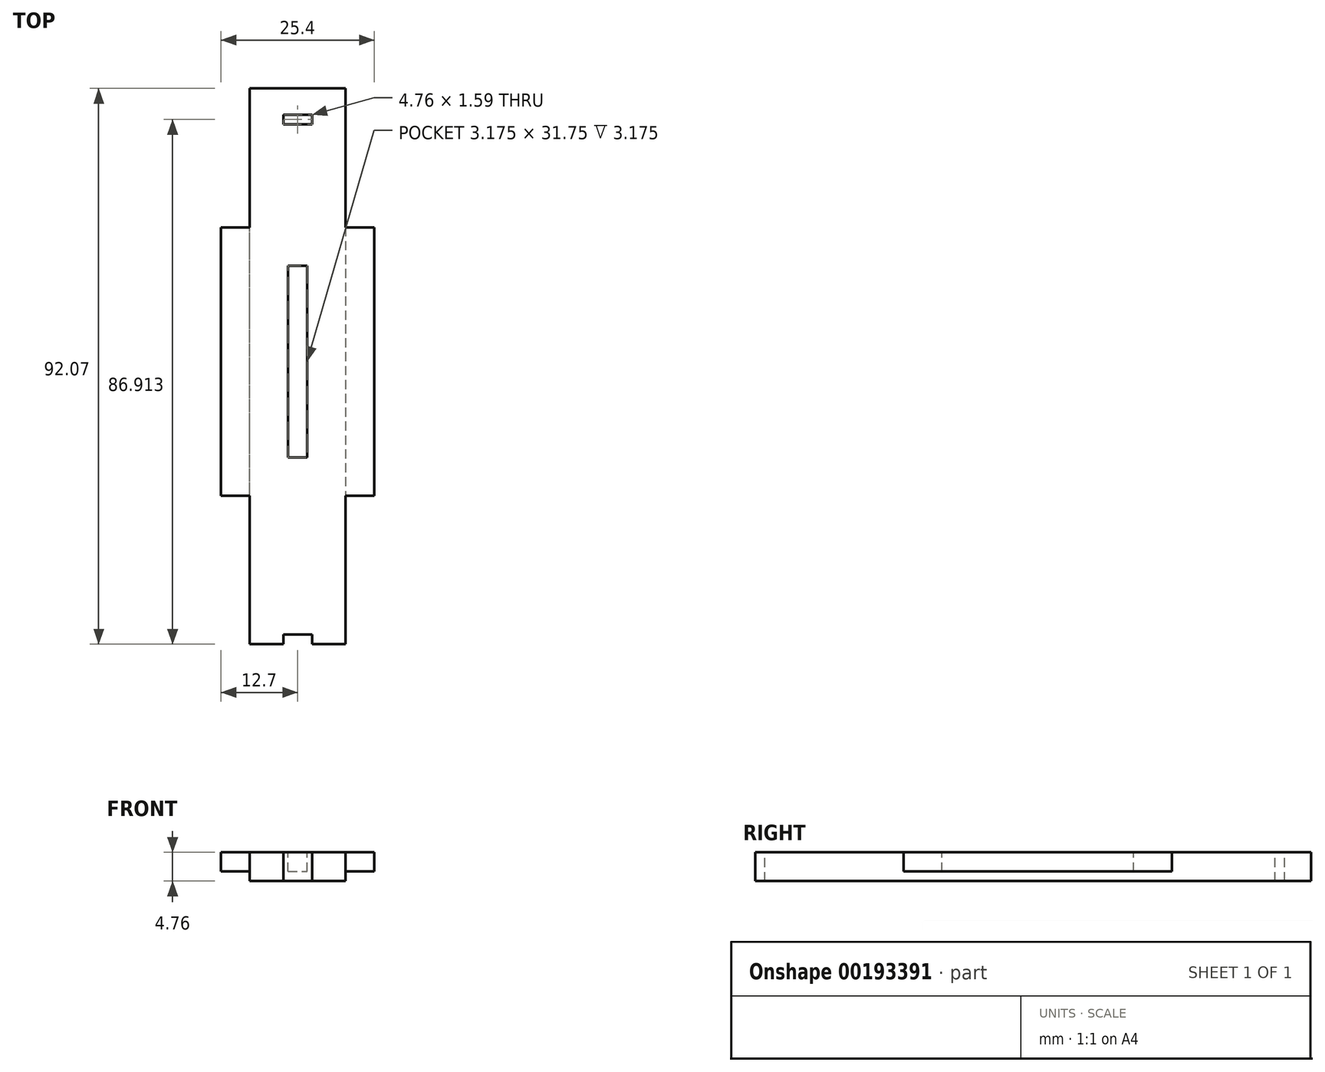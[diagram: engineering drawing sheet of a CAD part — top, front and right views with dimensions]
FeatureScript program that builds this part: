
annotation { "Feature Type Name" : "Feature", "Feature Type Description" : "" }
export const myFeature = defineFeature(function(context is Context, id is Id, definition is map)
    precondition{}
    {
        {
            var Q0;
            Q0=qCreatedBy(makeId("Top.planeOp"),FACE);
            var sketch = newSketch(context, id + "F0", { "sketchPlane" : qUnion([Q0])});
            skLineSegment(sketch, "E0", {"start": v(-7.94, 49.21) * mm, "end": v(7.94, 49.21) * mm});
            skLineSegment(sketch, "E1", {"start": v(7.94, 49.21) * mm, "end": v(7.94, 26.2) * mm});
            skLineSegment(sketch, "E2", {"start": v(7.94, 26.2) * mm, "end": v(12.7, 26.2) * mm});
            skLineSegment(sketch, "E3", {"start": v(12.7, 26.2) * mm, "end": v(12.7, -18.26) * mm});
            skLineSegment(sketch, "E4", {"start": v(12.7, -18.26) * mm, "end": v(7.94, -18.26) * mm});
            skLineSegment(sketch, "E5", {"start": v(7.94, -18.26) * mm, "end": v(7.94, -42.86) * mm});
            skLineSegment(sketch, "E6", {"start": v(7.94, -42.86) * mm, "end": v(-7.94, -42.86) * mm});
            skLineSegment(sketch, "E7", {"start": v(-7.94, -42.86) * mm, "end": v(-7.94, -18.26) * mm});
            skLineSegment(sketch, "E8", {"start": v(-7.94, -18.26) * mm, "end": v(-12.7, -18.26) * mm});
            skLineSegment(sketch, "E9", {"start": v(-12.7, -18.26) * mm, "end": v(-12.7, 26.2) * mm});
            skLineSegment(sketch, "E10", {"start": v(-12.7, 26.2) * mm, "end": v(-7.94, 26.2) * mm});
            skLineSegment(sketch, "E11", {"start": v(-7.94, 26.2) * mm, "end": v(-7.94, 49.21) * mm});
            skSolve(sketch);
        }
        {
            var Q0;
            Q0 = qSketchRegion(id + "F0", true);
            extrude(context, id + "F1", {"entities" : qUnion([Q0]), "depth" : 3.17 * mm});
        }
        {
            var Q0;
            Q0=makeQuery(id+"F1.opExtrude","CAP_FACE",FACE,{"disambiguationData":[OSD([sQuery(id+"F0.wireOp",EDGE,"E0"),sQuery(id+"F0.wireOp",EDGE,"E1"),sQuery(id+"F0.wireOp",EDGE,"E2"),sQuery(id+"F0.wireOp",EDGE,"E3"),sQuery(id+"F0.wireOp",EDGE,"E4"),sQuery(id+"F0.wireOp",EDGE,"E5"),sQuery(id+"F0.wireOp",EDGE,"E6"),sQuery(id+"F0.wireOp",EDGE,"E7"),sQuery(id+"F0.wireOp",EDGE,"E8"),sQuery(id+"F0.wireOp",EDGE,"E9"),sQuery(id+"F0.wireOp",EDGE,"E10"),sQuery(id+"F0.wireOp",EDGE,"E11")])],"isStart":true});
            var sketch = newSketch(context, id + "F2", { "sketchPlane" : qUnion([Q0])});
            skLineSegment(sketch, "E12.bottom", {"start": v(7.94, -49.21) * mm, "end": v(-7.94, -49.21) * mm});
            skLineSegment(sketch, "E12.top", {"start": v(7.94, 42.86) * mm, "end": v(-7.94, 42.86) * mm});
            skLineSegment(sketch, "E12.left", {"start": v(7.94, -49.21) * mm, "end": v(7.94, 42.86) * mm});
            skLineSegment(sketch, "E12.right", {"start": v(-7.94, -49.21) * mm, "end": v(-7.94, 42.86) * mm});
            skSolve(sketch);
        }
        {
            var Q0;
            Q0 = qSketchRegion(id + "F2", true);
            extrude(context, id + "F3", {"entities" : qUnion([Q0]), "operationType" : NewBodyOperationType.ADD, "depth" : 1.59 * mm});
        }
        {
            var Q0;
            Q0=makeQuery(id+"F1.opExtrude","CAP_FACE",FACE,{"disambiguationData":[OSD([sQuery(id+"F0.wireOp",EDGE,"E0"),sQuery(id+"F0.wireOp",EDGE,"E1"),sQuery(id+"F0.wireOp",EDGE,"E2"),sQuery(id+"F0.wireOp",EDGE,"E3"),sQuery(id+"F0.wireOp",EDGE,"E4"),sQuery(id+"F0.wireOp",EDGE,"E5"),sQuery(id+"F0.wireOp",EDGE,"E6"),sQuery(id+"F0.wireOp",EDGE,"E7"),sQuery(id+"F0.wireOp",EDGE,"E8"),sQuery(id+"F0.wireOp",EDGE,"E9"),sQuery(id+"F0.wireOp",EDGE,"E10"),sQuery(id+"F0.wireOp",EDGE,"E11")])],"isStart":false});
            var sketch = newSketch(context, id + "F4", { "sketchPlane" : qUnion([Q0])});
            skLineSegment(sketch, "E13.bottom", {"start": v(-1.59, 19.84) * mm, "end": v(1.59, 19.84) * mm});
            skLineSegment(sketch, "E13.top", {"start": v(-1.59, -11.9) * mm, "end": v(1.59, -11.9) * mm});
            skLineSegment(sketch, "E13.left", {"start": v(-1.59, 19.84) * mm, "end": v(-1.59, -11.9) * mm});
            skLineSegment(sketch, "E13.right", {"start": v(1.59, 19.84) * mm, "end": v(1.59, -11.9) * mm});
            skSolve(sketch);
        }
        {
            var Q0;
            Q0 = qSketchRegion(id + "F4", true);
            extrude(context, id + "F5", {"entities" : qUnion([Q0]), "operationType" : NewBodyOperationType.REMOVE, "oppositeDirection" : true, "depth" : 3.17 * mm});
        }
        {
            var Q0;
            Q0=makeQuery(id+"F1.opExtrude","CAP_FACE",FACE,{"disambiguationData":[OSD([sQuery(id+"F0.wireOp",EDGE,"E0"),sQuery(id+"F0.wireOp",EDGE,"E1"),sQuery(id+"F0.wireOp",EDGE,"E2"),sQuery(id+"F0.wireOp",EDGE,"E3"),sQuery(id+"F0.wireOp",EDGE,"E4"),sQuery(id+"F0.wireOp",EDGE,"E5"),sQuery(id+"F0.wireOp",EDGE,"E6"),sQuery(id+"F0.wireOp",EDGE,"E7"),sQuery(id+"F0.wireOp",EDGE,"E8"),sQuery(id+"F0.wireOp",EDGE,"E9"),sQuery(id+"F0.wireOp",EDGE,"E10"),sQuery(id+"F0.wireOp",EDGE,"E11")])],"isStart":false});
            var sketch = newSketch(context, id + "F6", { "sketchPlane" : qUnion([Q0])});
            skLineSegment(sketch, "E14.bottom", {"start": v(-2.38, -42.86) * mm, "end": v(2.38, -42.86) * mm});
            skLineSegment(sketch, "E14.top", {"start": v(-2.38, -41.27) * mm, "end": v(2.38, -41.27) * mm});
            skLineSegment(sketch, "E14.left", {"start": v(-2.38, -42.86) * mm, "end": v(-2.38, -41.27) * mm});
            skLineSegment(sketch, "E14.right", {"start": v(2.38, -42.86) * mm, "end": v(2.38, -41.27) * mm});
            skSolve(sketch);
        }
        {
            var Q0;
            Q0 = qSketchRegion(id + "F6", true);
            extrude(context, id + "F7", {"entities" : qUnion([Q0]), "operationType" : NewBodyOperationType.REMOVE, "endBound" : BoundingType.THROUGH_ALL, "oppositeDirection" : true, "depth" : 25.4 * mm});
        }
        {
            var Q0;
            Q0=makeQuery(id+"F1.opExtrude","CAP_FACE",FACE,{"disambiguationData":[OSD([sQuery(id+"F0.wireOp",EDGE,"E0"),sQuery(id+"F0.wireOp",EDGE,"E1"),sQuery(id+"F0.wireOp",EDGE,"E2"),sQuery(id+"F0.wireOp",EDGE,"E3"),sQuery(id+"F0.wireOp",EDGE,"E4"),sQuery(id+"F0.wireOp",EDGE,"E5"),sQuery(id+"F0.wireOp",EDGE,"E6"),sQuery(id+"F0.wireOp",EDGE,"E7"),sQuery(id+"F0.wireOp",EDGE,"E8"),sQuery(id+"F0.wireOp",EDGE,"E9"),sQuery(id+"F0.wireOp",EDGE,"E10"),sQuery(id+"F0.wireOp",EDGE,"E11")])],"isStart":false});
            var sketch = newSketch(context, id + "F8", { "sketchPlane" : qUnion([Q0])});
            skLineSegment(sketch, "E15.bottom", {"start": v(-2.38, 43.26) * mm, "end": v(2.38, 43.26) * mm});
            skLineSegment(sketch, "E15.top", {"start": v(-2.38, 44.85) * mm, "end": v(2.38, 44.85) * mm});
            skLineSegment(sketch, "E15.left", {"start": v(-2.38, 43.26) * mm, "end": v(-2.38, 44.85) * mm});
            skLineSegment(sketch, "E15.right", {"start": v(2.38, 43.26) * mm, "end": v(2.38, 44.85) * mm});
            skSolve(sketch);
        }
        {
            var Q0;
            Q0 = qSketchRegion(id + "F8", true);
            extrude(context, id + "F9", {"entities" : qUnion([Q0]), "operationType" : NewBodyOperationType.REMOVE, "endBound" : BoundingType.THROUGH_ALL, "oppositeDirection" : true, "depth" : 25.4 * mm});
        }
    });
